# Revit family: Faucet-Valves_and_Controls-KOHLER-Beam-K-25150IN
name_source: partatom
category: Plumbing Fixtures
units: mm (PartAtom-declared; Revit-internal decimal feet)

## family parameters
Cut with Voids When Loaded = No
Host = Face
OmniClass Number = 23.27.31.00
OmniClass Title = Valves
Part Type = Normal
Room Calculation Point = No
Round Connector Dimension = Use Diameter
Shared = No

## types (1)
- NA-Not Apllicable
    ADA Compliant = No
    Assembly Code = D2020
    CW Connection = Yes
    Cold Water Inlet = Cold Water Inlet
    Date Modified = 01/01/2023
    Default Elevation = 36"
    Description = Single Control Wall Mount Valve
    Drain Included = No
    Faucet Hole Spacing = 0"
    Finish = Kohler-Metal-Brass
    Flow Rate = 0 GPM
    HW Connection = Yes
    Handle Clearance = 0"
    Height = 2"
    Hot Water Inlet = Hot Water Inlet
    Length = 4 1/4"
    Manufacturer = Kohler Co.
    Master Format 2014 = 23 09 13.33
    Master Format 2014 Name = Control Valves
    Material = Premium Metal Construction
    Model = K-25150IN-NA
    Pressure = 0.00 psi
    Product Name = Beam
    Product Page URL = https://www.kohler.co.in
    Spout Reach = 0"
    Tempered Water Outlet = Tempered Water Outlet
    Type = 1
    URL = https://www.kohler.co.in
    Vent Connection = No
    Waste Connection = No
    Waste Water Outlet = Waste Water Outlet
    WaterSense Certified = No
    Width = 6 1/16"

## geometry (parser evidence)
native form markers: Sweep x5
no freeform markers — native parametric forms only
